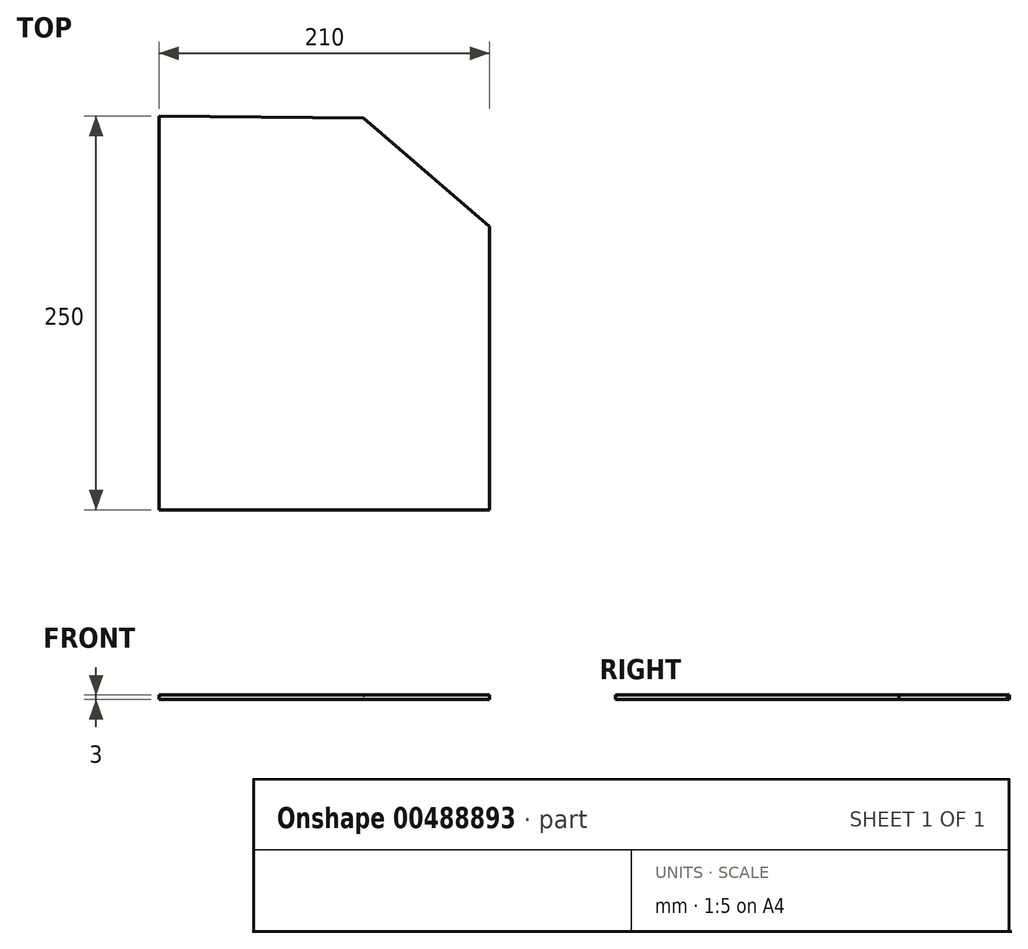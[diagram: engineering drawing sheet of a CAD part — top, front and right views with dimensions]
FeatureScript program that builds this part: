
annotation { "Feature Type Name" : "Feature", "Feature Type Description" : "" }
export const myFeature = defineFeature(function(context is Context, id is Id, definition is map)
    precondition{}
    {
        {
            var Q0;
            Q0=qCreatedBy(makeId("Top.planeOp"),FACE);
            var sketch = newSketch(context, id + "F0", { "sketchPlane" : qUnion([Q0])});
            skLineSegment(sketch, "E0", {"start": v(-210, 114.7) * mm, "end": v(-210, -135.3) * mm});
            skLineSegment(sketch, "E1", {"start": v(-210, -135.3) * mm, "end": v(0, -135.3) * mm});
            skLineSegment(sketch, "E2", {"start": v(0, -135.3) * mm, "end": v(0, 44.7) * mm});
            skLineSegment(sketch, "E3", {"start": v(0, 44.7) * mm, "end": v(-80, 113.6) * mm});
            skLineSegment(sketch, "E4", {"start": v(-210, 114.7) * mm, "end": v(-80, 113.6) * mm});
            skSolve(sketch);
        }
        {
            var Q0;
            Q0=makeQuery(id+"F0.imprint","IMPRINT",FACE,{"disambiguationData":[TD([[makeQuery(id+"F0.imprint","IMPRINT",EDGE,{"derivedFrom":sQuery(id+"F0.wireOp",EDGE,"E0")}),1.0]])]});
            extrude(context, id + "F1", {"entities" : qUnion([Q0]), "depth" : 3 * mm});
        }
    });
